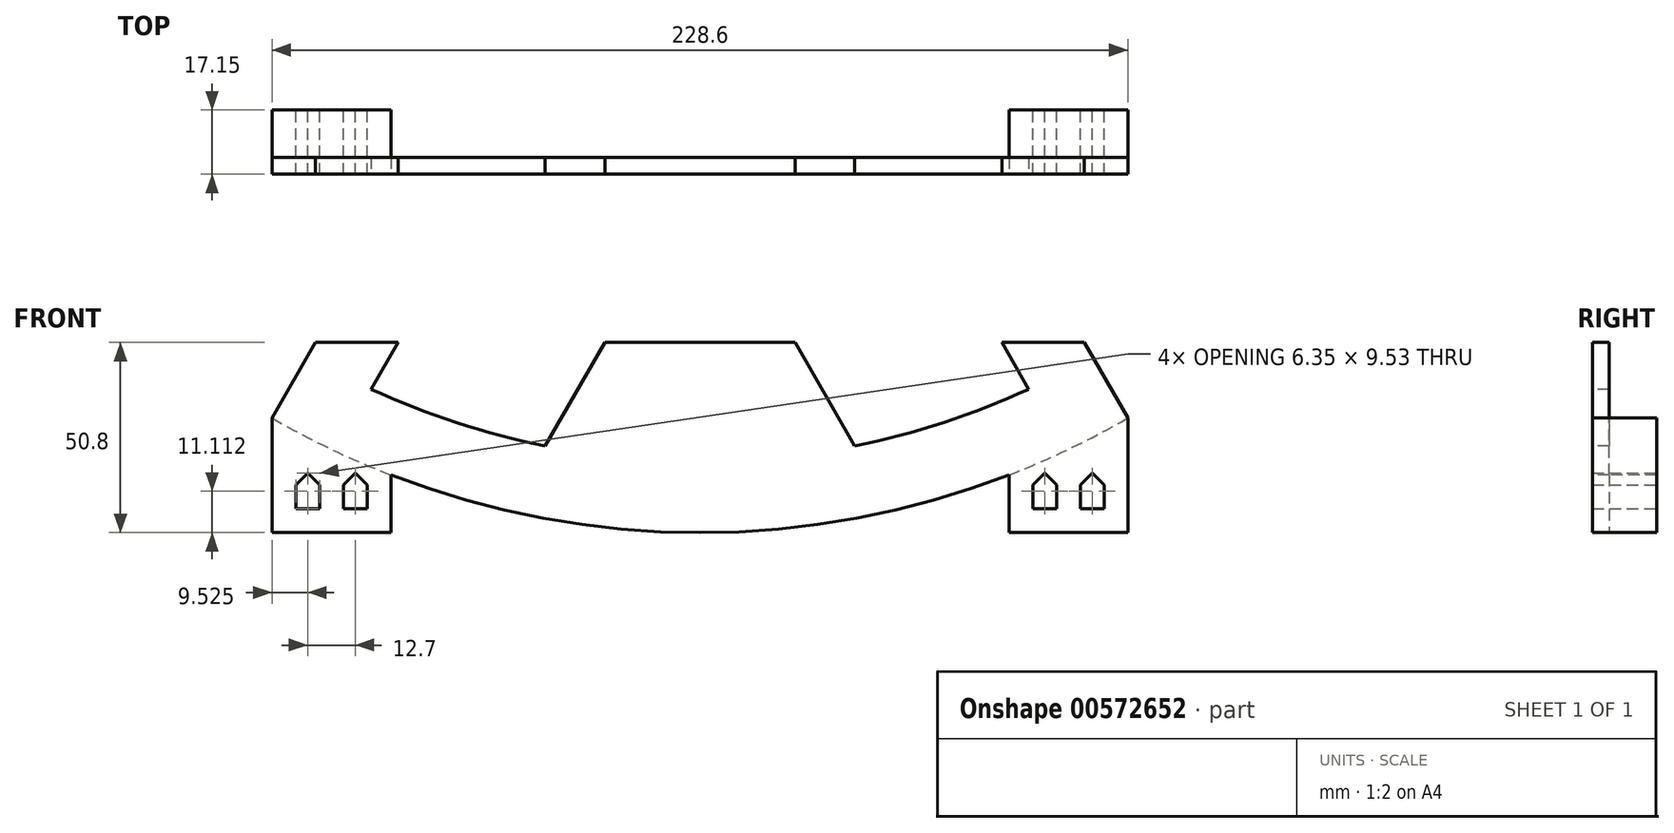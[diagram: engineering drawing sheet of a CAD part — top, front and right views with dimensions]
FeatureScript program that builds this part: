
annotation { "Feature Type Name" : "Feature", "Feature Type Description" : "" }
export const myFeature = defineFeature(function(context is Context, id is Id, definition is map)
    precondition{}
    {
        {
            var Q0;
            Q0=qCreatedBy(makeId("Front.planeOp"),FACE);
            var sketch = newSketch(context, id + "F0", { "sketchPlane" : qUnion([Q0])});
            skArc(sketch, "E0", {"start": v(-228.6, 0) * mm, "mid": v(0, -228.6) * mm, "end": v(228.6, 0) * mm});
            skLineSegment(sketch, "E1", {"start": v(-38.1, 0) * mm, "end": v(-228.6, 0) * mm});
            skLineSegment(sketch, "E2", {"start": v(38.1, 0) * mm, "end": v(228.6, 0) * mm});
            skLineSegment(sketch, "E3", {"start": v(-19.05, -33) * mm, "end": v(-114.3, -197.97) * mm});
            skLineSegment(sketch, "E4", {"start": v(19.05, -33) * mm, "end": v(114.3, -197.97) * mm});
            skArc(sketch, "E5", {"start": v(19.05, -33) * mm, "mid": v(0, 38.1) * mm, "end": v(-19.05, -33) * mm});
            skSolve(sketch);
        }
        {
            var Q0;
            {var subQ3=sQuery(id+"F0.wireOp",EDGE,"E3");Q0=makeQuery(id+"F0.imprint","IMPRINT",FACE,{"disambiguationData":[TD([[makeQuery(id+"F0.imprint","IMPRINT",EDGE,{"derivedFrom":subQ3}),1.0]])]});}
            extrude(context, id + "F1", {"entities" : qUnion([Q0]), "depth" : 127 * mm, "offsetDistance" : 25.4 * mm});
        }
        {
            var Q0;
            Q0=makeQuery(id+"F1.opExtrude","SWEPT_FACE",FACE,{"disambiguationData":[OSD([sQuery(id+"F0.wireOp",EDGE,"E5")])]});
            var Q1;
            Q1=makeQuery(id+"F1.opExtrude","SWEPT_FACE",FACE,{"disambiguationData":[OSD([sQuery(id+"F0.wireOp",EDGE,"E4")])]});
            var Q2;
            Q2=makeQuery(id+"F1.opExtrude","SWEPT_FACE",FACE,{"disambiguationData":[OSD([sQuery(id+"F0.wireOp",EDGE,"E3")])]});
            shell(context, id + "F2", {"entities" : qUnion([Q0, Q1, Q2]), "thickness" : 4.44 * mm});
        }
        {
            var Q0;
            Q0=makeQuery(id+"F1.opExtrude","CAP_FACE",FACE,{"disambiguationData":[OSD([sQuery(id+"F0.wireOp",EDGE,"E0"),sQuery(id+"F0.wireOp",EDGE,"E3"),sQuery(id+"F0.wireOp",EDGE,"E4"),sQuery(id+"F0.wireOp",EDGE,"E5")])],"isStart":false});
            var sketch = newSketch(context, id + "F3", { "sketchPlane" : qUnion([Q0])});
            skLineSegment(sketch, "E6.0", {"start": v(7.05, -50.3) * mm, "end": v(87.84, -190.25) * mm});
            skArc(sketch, "E6.1", {"start": v(-87.84, -190.25) * mm, "mid": v(-48.4, -203.88) * mm, "end": v(-7.05, -209.43) * mm});
            skCircle(sketch, "E7", {"center": v(0, 0) * mm, "radius": 9.53 * mm});
            skLineSegment(sketch, "E8", {"start": v(-7.05, -50.3) * mm, "end": v(-7.05, -125.9) * mm});
            skLineSegment(sketch, "E9", {"start": v(7.05, -50.3) * mm, "end": v(7.05, -125.9) * mm});
            skLineSegment(sketch, "E10", {"start": v(-87.84, -190.25) * mm, "end": v(-50.62, -125.78) * mm});
            skPoint(sketch, "E11.endSnap0", {"position": v(-66.67, -115.48) * mm});
            skLineSegment(sketch, "E12", {"start": v(-44.27, -114.78) * mm, "end": v(-14.9, -131.73) * mm});
            skLineSegment(sketch, "E13.trimOffspring", {"start": v(-7.05, -169.35) * mm, "end": v(-7.05, -209.43) * mm});
            skLineSegment(sketch, "E14.trimOffspring", {"start": v(-50.62, -125.78) * mm, "end": v(-87.84, -190.25) * mm});
            skArc(sketch, "E15.trimOffspring", {"start": v(7.05, -209.43) * mm, "mid": v(48.4, -203.88) * mm, "end": v(87.84, -190.25) * mm});
            skLineSegment(sketch, "E16", {"start": v(-7.05, -50.3) * mm, "end": v(0, -50.3) * mm, "construction": true});
            skLineSegment(sketch, "E17", {"start": v(0, -50.3) * mm, "end": v(0, -85.39) * mm, "construction": true});
            skLineSegment(sketch, "E18", {"start": v(-44.27, -114.78) * mm, "end": v(-7.05, -50.3) * mm});
            skLineSegment(sketch, "E19.MirrorCS", {"start": v(44.27, -114.78) * mm, "end": v(14.9, -131.73) * mm});
            skLineSegment(sketch, "E20.trimOffspring", {"start": v(7.05, -169.35) * mm, "end": v(7.05, -209.43) * mm});
            skArc(sketch, "E21", {"start": v(14.9, -131.73) * mm, "mid": v(11.36, -128.3) * mm, "end": v(7.05, -125.9) * mm});
            skPoint(sketch, "E22.orphan", {"position": v(7.05, -136.27) * mm});
            skPoint(sketch, "E23.orphan", {"position": v(7.05, -150.93) * mm});
            skPoint(sketch, "E24.orphan", {"position": v(-7.05, -150.93) * mm});
            skPoint(sketch, "E25.orphan", {"position": v(-7.05, -136.27) * mm});
            skLineSegment(sketch, "E26", {"start": v(50.62, -125.78) * mm, "end": v(7.05, -169.35) * mm, "construction": true});
            skLineSegment(sketch, "E27", {"start": v(50.62, -125.78) * mm, "end": v(7.05, -169.35) * mm});
            skLineSegment(sketch, "E28.MirrorCS", {"start": v(-50.62, -125.78) * mm, "end": v(-7.05, -169.35) * mm});
            skArc(sketch, "E29.trimOffspring", {"start": v(-7.05, -125.9) * mm, "mid": v(-11.36, -128.3) * mm, "end": v(-14.9, -131.73) * mm});
            skSolve(sketch);
        }
        {
            var Q0;
            Q0=makeQuery(id+"F3.imprint","IMPRINT",FACE,{"disambiguationData":[TD([[makeQuery(id+"F3.imprint","IMPRINT",EDGE,{"derivedFrom":sQuery(id+"F3.wireOp",EDGE,"E6.1")}),1.0]])]});
            var Q1;
            {var subQ2=sQuery(id+"F3.wireOp",EDGE,"E15.trimOffspring");Q1=makeQuery(id+"F3.imprint","IMPRINT",FACE,{"disambiguationData":[TD([[makeQuery(id+"F3.imprint","IMPRINT",EDGE,{"derivedFrom":subQ2}),1.0]])]});}
            var Q2;
            {var subQ0=sQuery(id+"F3.wireOp",EDGE,"E9");Q2=makeQuery(id+"F3.imprint","IMPRINT",FACE,{"disambiguationData":[TD([[makeQuery(id+"F3.imprint","IMPRINT",EDGE,{"derivedFrom":subQ0}),1.0]])]});}
            var Q3;
            {var subQ0=sQuery(id+"F3.wireOp",EDGE,"E8");Q3=makeQuery(id+"F3.imprint","IMPRINT",FACE,{"disambiguationData":[TD([[makeQuery(id+"F3.imprint","IMPRINT",EDGE,{"derivedFrom":subQ0}),-1.0]])]});}
            var Q4;
            Q4=makeQuery(id+"F3.imprint","IMPRINT",FACE,{"disambiguationData":[TD([[makeQuery(id+"F3.imprint","IMPRINT",EDGE,{"derivedFrom":sQuery(id+"F3.wireOp",EDGE,"E7")}),1.0]])]});
            var Q5;
            Q5=makeQuery(id+"F1.opExtrude","CAP_FACE",FACE,{"disambiguationData":[OSD([sQuery(id+"F0.wireOp",EDGE,"E0"),sQuery(id+"F0.wireOp",EDGE,"E3"),sQuery(id+"F0.wireOp",EDGE,"E4"),sQuery(id+"F0.wireOp",EDGE,"E5")])],"isStart":true});
            extrude(context, id + "F4", {"entities" : qUnion([Q0, Q1, Q2, Q3, Q4]), "operationType" : NewBodyOperationType.REMOVE, "endBound" : BoundingType.UP_TO_SURFACE, "oppositeDirection" : true, "depth" : 25.4 * mm, "endBoundEntityFace" : qUnion([Q5]), "offsetDistance" : 25.4 * mm});
        }
        {
            var Q0;
            Q0=qCreatedBy(makeId("Front.planeOp"),FACE);
            var sketch = newSketch(context, id + "F5", { "sketchPlane" : qUnion([Q0])});
            skLineSegment(sketch, "E30", {"start": v(0, -228.6) * mm, "end": v(114.3, -228.6) * mm});
            skLineSegment(sketch, "E31", {"start": v(0, -228.6) * mm, "end": v(-114.3, -228.6) * mm});
            skLineSegment(sketch, "E32", {"start": v(114.3, -197.97) * mm, "end": v(114.3, -228.6) * mm});
            skLineSegment(sketch, "E33", {"start": v(-114.3, -197.97) * mm, "end": v(-114.3, -228.6) * mm});
            skPoint(sketch, "E34.orphan", {"position": v(-122.47, -228.6) * mm});
            skArc(sketch, "E35.0", {"start": v(-114.3, -197.97) * mm, "mid": v(0, -228.6) * mm, "end": v(114.3, -197.97) * mm});
            skLineSegment(sketch, "E36", {"start": v(114.3, -228.6) * mm, "end": v(107.95, -228.6) * mm, "construction": true});
            skLineSegment(sketch, "E37", {"start": v(107.95, -228.6) * mm, "end": v(107.95, -222.25) * mm, "construction": true});
            skLineSegment(sketch, "E38.bottom", {"start": v(107.95, -222.25) * mm, "end": v(101.6, -222.25) * mm});
            skLineSegment(sketch, "E38.left", {"start": v(107.95, -222.25) * mm, "end": v(107.95, -215.9) * mm});
            skLineSegment(sketch, "E38.right", {"start": v(88.9, -222.25) * mm, "end": v(88.9, -215.9) * mm});
            skLineSegment(sketch, "E39", {"start": v(101.6, -222.25) * mm, "end": v(101.6, -215.9) * mm});
            skLineSegment(sketch, "E40", {"start": v(95.25, -222.25) * mm, "end": v(95.25, -215.9) * mm});
            skLineSegment(sketch, "E41.trimOffspring", {"start": v(95.25, -222.25) * mm, "end": v(88.9, -222.25) * mm});
            skLineSegment(sketch, "E42", {"start": v(104.78, -215.9) * mm, "end": v(104.78, -212.72) * mm, "construction": true});
            skLineSegment(sketch, "E43", {"start": v(92.08, -215.9) * mm, "end": v(92.08, -212.72) * mm, "construction": true});
            skLineSegment(sketch, "E44", {"start": v(107.95, -215.9) * mm, "end": v(104.78, -212.72) * mm});
            skLineSegment(sketch, "E45", {"start": v(101.6, -215.9) * mm, "end": v(104.78, -212.72) * mm});
            skLineSegment(sketch, "E46", {"start": v(95.25, -215.9) * mm, "end": v(92.08, -212.72) * mm});
            skLineSegment(sketch, "E47", {"start": v(88.9, -215.9) * mm, "end": v(92.08, -212.72) * mm});
            skLineSegment(sketch, "E48.MirrorCS", {"start": v(-104.78, -215.9) * mm, "end": v(-104.78, -212.72) * mm, "construction": true});
            skLineSegment(sketch, "E49.MirrorCS", {"start": v(-92.08, -215.9) * mm, "end": v(-92.08, -212.72) * mm, "construction": true});
            skLineSegment(sketch, "E50.MirrorCS", {"start": v(-101.6, -215.9) * mm, "end": v(-104.78, -212.72) * mm});
            skLineSegment(sketch, "E51.MirrorCS", {"start": v(-88.9, -215.9) * mm, "end": v(-92.08, -212.72) * mm});
            skLineSegment(sketch, "E52.MirrorCS", {"start": v(-107.95, -215.9) * mm, "end": v(-104.78, -212.72) * mm});
            skLineSegment(sketch, "E53.MirrorCS", {"start": v(-95.25, -222.25) * mm, "end": v(-95.25, -215.9) * mm});
            skLineSegment(sketch, "E54.MirrorCS", {"start": v(-101.6, -222.25) * mm, "end": v(-101.6, -215.9) * mm});
            skLineSegment(sketch, "E55.MirrorCS", {"start": v(-107.95, -222.25) * mm, "end": v(-107.95, -215.9) * mm});
            skLineSegment(sketch, "E56.MirrorCS", {"start": v(-107.95, -222.25) * mm, "end": v(-101.6, -222.25) * mm});
            skLineSegment(sketch, "E57.MirrorCS", {"start": v(-88.9, -222.25) * mm, "end": v(-88.9, -215.9) * mm});
            skLineSegment(sketch, "E58.MirrorCS", {"start": v(-95.25, -215.9) * mm, "end": v(-92.08, -212.72) * mm});
            skLineSegment(sketch, "E59.MirrorCS", {"start": v(-95.25, -222.25) * mm, "end": v(-88.9, -222.25) * mm});
            skSolve(sketch);
        }
        {
            var Q0;
            {var subQ2=sQuery(id+"F5.wireOp",EDGE,"E30");Q0=makeQuery(id+"F5.imprint","IMPRINT",FACE,{"disambiguationData":[TD([[makeQuery(id+"F5.imprint","IMPRINT",EDGE,{"derivedFrom":subQ2}),1.0]])]});}
            var Q1;
            {var subQ2=sQuery(id+"F5.wireOp",EDGE,"E31");Q1=makeQuery(id+"F5.imprint","IMPRINT",FACE,{"disambiguationData":[TD([[makeQuery(id+"F5.imprint","IMPRINT",EDGE,{"derivedFrom":subQ2}),-1.0]])]});}
            var Q2;
            Q2=makeQuery(id+"F1.opExtrude","CAP_FACE",FACE,{"disambiguationData":[OSD([sQuery(id+"F0.wireOp",EDGE,"E0"),sQuery(id+"F0.wireOp",EDGE,"E3"),sQuery(id+"F0.wireOp",EDGE,"E4"),sQuery(id+"F0.wireOp",EDGE,"E5")])],"isStart":false});
            extrude(context, id + "F6", {"entities" : qUnion([Q0, Q1]), "operationType" : NewBodyOperationType.ADD, "endBound" : BoundingType.UP_TO_SURFACE, "depth" : 25.4 * mm, "endBoundEntityFace" : qUnion([Q2]), "offsetDistance" : 25.4 * mm});
        }
        {
            var Q0;
            Q0=qCreatedBy(makeId("Front.planeOp"),FACE);
            var sketch = newSketch(context, id + "F7", { "sketchPlane" : qUnion([Q0])});
            skLineSegment(sketch, "E60", {"start": v(0, 0) * mm, "end": v(0, -177.8) * mm, "construction": true});
            skLineSegment(sketch, "E61", {"start": v(0, -177.8) * mm, "end": v(122.5, -177.8) * mm});
            skLineSegment(sketch, "E62", {"start": v(122.5, -177.8) * mm, "end": v(122.5, 99.95) * mm});
            skLineSegment(sketch, "E63", {"start": v(0, -177.8) * mm, "end": v(-155.13, -177.8) * mm});
            skLineSegment(sketch, "E64", {"start": v(-155.13, -177.8) * mm, "end": v(-155.13, 97.68) * mm});
            skLineSegment(sketch, "E65", {"start": v(-155.13, 97.68) * mm, "end": v(122.5, 99.95) * mm});
            skSolve(sketch);
        }
        {
            var Q0;
            Q0=makeQuery(id+"F7.imprint","IMPRINT",FACE,{"disambiguationData":[TD([[makeQuery(id+"F7.imprint","IMPRINT",EDGE,{"derivedFrom":sQuery(id+"F7.wireOp",EDGE,"E61")}),1.0]])]});
            extrude(context, id + "F8", {"entities" : qUnion([Q0]), "operationType" : NewBodyOperationType.REMOVE, "depth" : 154.94 * mm, "offsetDistance" : 25.4 * mm});
        }
        {
            var Q0;
            {var subQ0=sQuery(id+"F5.wireOp",EDGE,"E35.0");Q0=makeQuery(id+"F6.boolean.opBoolean","MERGE",FACE,{"derivedFrom":[makeQuery(id+"F1.opExtrude","CAP_FACE",FACE,{"disambiguationData":[OSD([sQuery(id+"F0.wireOp",EDGE,"E0"),sQuery(id+"F0.wireOp",EDGE,"E3"),sQuery(id+"F0.wireOp",EDGE,"E4"),sQuery(id+"F0.wireOp",EDGE,"E5")])],"isStart":true}),makeQuery(id+"F6.opExtrude","CAP_FACE",FACE,{"disambiguationData":[OSD([sQuery(id+"F5.wireOp",EDGE,"E30"),sQuery(id+"F5.wireOp",EDGE,"E32"),subQ0,sQuery(id+"F5.wireOp",EDGE,"E38.bottom"),sQuery(id+"F5.wireOp",EDGE,"E38.left"),sQuery(id+"F5.wireOp",EDGE,"E38.right"),sQuery(id+"F5.wireOp",EDGE,"E39"),sQuery(id+"F5.wireOp",EDGE,"E40"),sQuery(id+"F5.wireOp",EDGE,"E41.trimOffspring"),sQuery(id+"F5.wireOp",EDGE,"E44"),sQuery(id+"F5.wireOp",EDGE,"E45"),sQuery(id+"F5.wireOp",EDGE,"E46"),sQuery(id+"F5.wireOp",EDGE,"E47")])],"isStart":true}),makeQuery(id+"F6.opExtrude","CAP_FACE",FACE,{"disambiguationData":[OSD([sQuery(id+"F5.wireOp",EDGE,"E31"),sQuery(id+"F5.wireOp",EDGE,"E33"),subQ0,sQuery(id+"F5.wireOp",EDGE,"E50.MirrorCS"),sQuery(id+"F5.wireOp",EDGE,"E51.MirrorCS"),sQuery(id+"F5.wireOp",EDGE,"E52.MirrorCS"),sQuery(id+"F5.wireOp",EDGE,"E53.MirrorCS"),sQuery(id+"F5.wireOp",EDGE,"E54.MirrorCS"),sQuery(id+"F5.wireOp",EDGE,"E55.MirrorCS"),sQuery(id+"F5.wireOp",EDGE,"E56.MirrorCS"),sQuery(id+"F5.wireOp",EDGE,"E57.MirrorCS"),sQuery(id+"F5.wireOp",EDGE,"E58.MirrorCS"),sQuery(id+"F5.wireOp",EDGE,"E59.MirrorCS")])],"isStart":true})]});}
            var sketch = newSketch(context, id + "F9", { "sketchPlane" : qUnion([Q0])});
            skArc(sketch, "E66.0", {"start": v(-87.84, -190.25) * mm, "mid": v(-48.4, -203.88) * mm, "end": v(-7.05, -209.43) * mm});
            skLineSegment(sketch, "E67.0", {"start": v(-7.05, -209.43) * mm, "end": v(-7.05, -177.8) * mm});
            skLineSegment(sketch, "E68", {"start": v(0, -177.8) * mm, "end": v(25.4, -177.8) * mm});
            skLineSegment(sketch, "E69", {"start": v(0, -177.8) * mm, "end": v(-25.4, -177.8) * mm});
            skLineSegment(sketch, "E70", {"start": v(-25.4, -177.8) * mm, "end": v(-41.35, -205.43) * mm});
            skLineSegment(sketch, "E71", {"start": v(25.4, -177.8) * mm, "end": v(41.35, -205.43) * mm});
            skLineSegment(sketch, "E72.0", {"start": v(7.05, -209.43) * mm, "end": v(7.05, -177.8) * mm});
            skArc(sketch, "E73.0", {"start": v(7.05, -209.43) * mm, "mid": v(48.4, -203.88) * mm, "end": v(87.84, -190.25) * mm});
            skSolve(sketch);
        }
        {
            var Q0;
            {var subQ0=sQuery(id+"F9.wireOp",EDGE,"E67.0");Q0=makeQuery(id+"F9.imprint","IMPRINT",FACE,{"disambiguationData":[TD([[makeQuery(id+"F9.imprint","IMPRINT",EDGE,{"derivedFrom":subQ0}),1.0]])]});}
            var Q1;
            {var subQ2=sQuery(id+"F9.wireOp",EDGE,"E71");Q1=makeQuery(id+"F9.imprint","IMPRINT",FACE,{"disambiguationData":[TD([[makeQuery(id+"F9.imprint","IMPRINT",EDGE,{"derivedFrom":subQ2}),-1.0]])]});}
            var Q2;
            {var subQ0=sQuery(id+"F0.wireOp",EDGE,"E5");var subQ1=sQuery(id+"F0.wireOp",EDGE,"E4");var subQ2=sQuery(id+"F0.wireOp",EDGE,"E3");var subQ3=sQuery(id+"F0.wireOp",EDGE,"E0");Q2=makeQuery(id+"F2.opShell","OFFSET_FACE",FACE,{"disambiguationData":[OSD([subQ3,subQ2,subQ1,subQ0]),TDD([makeQuery(id+"F1.opExtrude","CAP_FACE",FACE,{"disambiguationData":[OSD([subQ3,subQ2,subQ1,subQ0])],"isStart":true})])]});}
            extrude(context, id + "F10", {"entities" : qUnion([Q0, Q1]), "operationType" : NewBodyOperationType.ADD, "endBound" : BoundingType.UP_TO_SURFACE, "oppositeDirection" : true, "depth" : 25.4 * mm, "endBoundEntityFace" : qUnion([Q2]), "offsetDistance" : 25.4 * mm});
        }
        {
            var Q0;
            Q0=qCreatedBy(makeId("Front.planeOp"),FACE);
            var Q1;
            {var subQ0=sQuery(id+"F0.wireOp",EDGE,"E5");var subQ1=sQuery(id+"F0.wireOp",EDGE,"E4");var subQ2=sQuery(id+"F0.wireOp",EDGE,"E3");var subQ3=sQuery(id+"F0.wireOp",EDGE,"E0");Q1=makeQuery(id+"F6.boolean.opBoolean","MERGE",FACE,{"derivedFrom":[makeQuery(id+"F1.opExtrude","CAP_FACE",FACE,{"disambiguationData":[OSD([subQ3,subQ2,subQ1,subQ0])],"isStart":false}),makeQuery(id+"F6.opExtrude","CAP_FACE",FACE,{"disambiguationData":[OSD([subQ3,subQ2,subQ1,subQ0]),OD(0.0)],"isStart":false}),makeQuery(id+"F6.opExtrude","CAP_FACE",FACE,{"disambiguationData":[OSD([subQ3,subQ2,subQ1,subQ0]),OD(1.0)],"isStart":false})]});}
            cPlane(context, id + "F11", {"entities" : qUnion([Q0, Q1]), "cplaneType" : CPlaneType.MID_PLANE, "offset" : 25.4 * mm, "width" : 152.4 * mm, "height" : 152.4 * mm});
        }
        {
            var Q0;
            Q0=makeQuery(id+"F1.opExtrude","SWEPT_BODY",BODY,{"disambiguationData":[OSD([sQuery(id+"F0.wireOp",EDGE,"E0"),sQuery(id+"F0.wireOp",EDGE,"E3"),sQuery(id+"F0.wireOp",EDGE,"E4"),sQuery(id+"F0.wireOp",EDGE,"E5")])]});
            var Q1;
            Q1=qCreatedBy(id+"F11.planeOp",FACE);
            mirror(context, id + "F12", {"operationType" : NewBodyOperationType.ADD, "entities" : qUnion([Q0]), "mirrorPlane" : qUnion([Q1])});
        }
        {
            var Q0;
            {var subQ0=sQuery(id+"F5.wireOp",EDGE,"E35.0");var subQ1=sQuery(id+"F0.wireOp",EDGE,"E5");var subQ2=sQuery(id+"F0.wireOp",EDGE,"E4");var subQ3=sQuery(id+"F0.wireOp",EDGE,"E3");var subQ4=sQuery(id+"F0.wireOp",EDGE,"E0");Q0=makeQuery(id+"F12.boolean.opBoolean","MERGE",FACE,{"derivedFrom":[makeQuery(id+"F6.boolean.opBoolean","MERGE",FACE,{"derivedFrom":[makeQuery(id+"F1.opExtrude","CAP_FACE",FACE,{"disambiguationData":[OSD([subQ4,subQ3,subQ2,subQ1])],"isStart":false}),makeQuery(id+"F6.opExtrude","CAP_FACE",FACE,{"disambiguationData":[OSD([subQ4,subQ3,subQ2,subQ1]),OD(0.0)],"isStart":false}),makeQuery(id+"F6.opExtrude","CAP_FACE",FACE,{"disambiguationData":[OSD([subQ4,subQ3,subQ2,subQ1]),OD(1.0)],"isStart":false})]}),makeQuery(id+"F12.opPattern","COPY",FACE,{"derivedFrom":makeQuery(id+"F10.boolean.opBoolean","MERGE",FACE,{"derivedFrom":[makeQuery(id+"F6.boolean.opBoolean","MERGE",FACE,{"derivedFrom":[makeQuery(id+"F1.opExtrude","CAP_FACE",FACE,{"disambiguationData":[OSD([subQ4,subQ3,subQ2,subQ1])],"isStart":true}),makeQuery(id+"F6.opExtrude","CAP_FACE",FACE,{"disambiguationData":[OSD([sQuery(id+"F5.wireOp",EDGE,"E30"),sQuery(id+"F5.wireOp",EDGE,"E32"),subQ0,sQuery(id+"F5.wireOp",EDGE,"E38.bottom"),sQuery(id+"F5.wireOp",EDGE,"E38.left"),sQuery(id+"F5.wireOp",EDGE,"E38.right"),sQuery(id+"F5.wireOp",EDGE,"E39"),sQuery(id+"F5.wireOp",EDGE,"E40"),sQuery(id+"F5.wireOp",EDGE,"E41.trimOffspring"),sQuery(id+"F5.wireOp",EDGE,"E44"),sQuery(id+"F5.wireOp",EDGE,"E45"),sQuery(id+"F5.wireOp",EDGE,"E46"),sQuery(id+"F5.wireOp",EDGE,"E47")])],"isStart":true}),makeQuery(id+"F6.opExtrude","CAP_FACE",FACE,{"disambiguationData":[OSD([sQuery(id+"F5.wireOp",EDGE,"E31"),sQuery(id+"F5.wireOp",EDGE,"E33"),subQ0,sQuery(id+"F5.wireOp",EDGE,"E50.MirrorCS"),sQuery(id+"F5.wireOp",EDGE,"E51.MirrorCS"),sQuery(id+"F5.wireOp",EDGE,"E52.MirrorCS"),sQuery(id+"F5.wireOp",EDGE,"E53.MirrorCS"),sQuery(id+"F5.wireOp",EDGE,"E54.MirrorCS"),sQuery(id+"F5.wireOp",EDGE,"E55.MirrorCS"),sQuery(id+"F5.wireOp",EDGE,"E56.MirrorCS"),sQuery(id+"F5.wireOp",EDGE,"E57.MirrorCS"),sQuery(id+"F5.wireOp",EDGE,"E58.MirrorCS"),sQuery(id+"F5.wireOp",EDGE,"E59.MirrorCS")])],"isStart":true})]}),makeQuery(id+"F10.opExtrude","CAP_FACE",FACE,{"disambiguationData":[OSD([sQuery(id+"F9.wireOp",EDGE,"E66.0"),sQuery(id+"F9.wireOp",EDGE,"E67.0"),sQuery(id+"F9.wireOp",EDGE,"E69"),sQuery(id+"F9.wireOp",EDGE,"E70")])],"isStart":true}),makeQuery(id+"F10.opExtrude","CAP_FACE",FACE,{"disambiguationData":[OSD([sQuery(id+"F9.wireOp",EDGE,"E68"),sQuery(id+"F9.wireOp",EDGE,"E71"),sQuery(id+"F9.wireOp",EDGE,"E72.0"),sQuery(id+"F9.wireOp",EDGE,"E73.0")])],"isStart":true})]}),"instanceName":"1"})]});}
            var sketch = newSketch(context, id + "F13", { "sketchPlane" : qUnion([Q0])});
            skArc(sketch, "E74", {"start": v(-114.3, -197.97) * mm, "mid": v(0, -228.6) * mm, "end": v(114.3, -197.97) * mm});
            skLineSegment(sketch, "E75.0", {"start": v(114.3, -228.6) * mm, "end": v(-114.3, -228.6) * mm});
            skLineSegment(sketch, "E76", {"start": v(-82.55, -228.6) * mm, "end": v(-82.55, -213.17) * mm});
            skLineSegment(sketch, "E77.MirrorCS", {"start": v(82.55, -228.6) * mm, "end": v(82.55, -213.17) * mm});
            skArc(sketch, "E78.MirrorCS", {"start": v(114.3, -197.97) * mm, "mid": v(0, -228.6) * mm, "end": v(-114.3, -197.97) * mm});
            skLineSegment(sketch, "E79.MirrorCS", {"start": v(-114.3, -228.6) * mm, "end": v(114.3, -228.6) * mm});
            skSolve(sketch);
        }
        {
            var Q0;
            {var subQ0=sQuery(id+"F13.wireOp",EDGE,"E76");Q0=makeQuery(id+"F13.imprint","IMPRINT",FACE,{"disambiguationData":[TD([[makeQuery(id+"F13.imprint","IMPRINT",EDGE,{"derivedFrom":subQ0}),-1.0]])]});}
            var Q1;
            {var subQ0=sQuery(id+"F13.wireOp",EDGE,"E77.MirrorCS");Q1=makeQuery(id+"F13.imprint","IMPRINT",FACE,{"disambiguationData":[TD([[makeQuery(id+"F13.imprint","IMPRINT",EDGE,{"derivedFrom":subQ0}),1.0]])]});}
            var Q2;
            {var subQ0=sQuery(id+"F5.wireOp",EDGE,"E35.0");Q2=makeQuery(id+"F10.boolean.opBoolean","MERGE",FACE,{"derivedFrom":[makeQuery(id+"F6.boolean.opBoolean","MERGE",FACE,{"derivedFrom":[makeQuery(id+"F1.opExtrude","CAP_FACE",FACE,{"disambiguationData":[OSD([sQuery(id+"F0.wireOp",EDGE,"E0"),sQuery(id+"F0.wireOp",EDGE,"E3"),sQuery(id+"F0.wireOp",EDGE,"E4"),sQuery(id+"F0.wireOp",EDGE,"E5")])],"isStart":true}),makeQuery(id+"F6.opExtrude","CAP_FACE",FACE,{"disambiguationData":[OSD([sQuery(id+"F5.wireOp",EDGE,"E30"),sQuery(id+"F5.wireOp",EDGE,"E32"),subQ0,sQuery(id+"F5.wireOp",EDGE,"E38.bottom"),sQuery(id+"F5.wireOp",EDGE,"E38.left"),sQuery(id+"F5.wireOp",EDGE,"E38.right"),sQuery(id+"F5.wireOp",EDGE,"E39"),sQuery(id+"F5.wireOp",EDGE,"E40"),sQuery(id+"F5.wireOp",EDGE,"E41.trimOffspring"),sQuery(id+"F5.wireOp",EDGE,"E44"),sQuery(id+"F5.wireOp",EDGE,"E45"),sQuery(id+"F5.wireOp",EDGE,"E46"),sQuery(id+"F5.wireOp",EDGE,"E47")])],"isStart":true}),makeQuery(id+"F6.opExtrude","CAP_FACE",FACE,{"disambiguationData":[OSD([sQuery(id+"F5.wireOp",EDGE,"E31"),sQuery(id+"F5.wireOp",EDGE,"E33"),subQ0,sQuery(id+"F5.wireOp",EDGE,"E50.MirrorCS"),sQuery(id+"F5.wireOp",EDGE,"E51.MirrorCS"),sQuery(id+"F5.wireOp",EDGE,"E52.MirrorCS"),sQuery(id+"F5.wireOp",EDGE,"E53.MirrorCS"),sQuery(id+"F5.wireOp",EDGE,"E54.MirrorCS"),sQuery(id+"F5.wireOp",EDGE,"E55.MirrorCS"),sQuery(id+"F5.wireOp",EDGE,"E56.MirrorCS"),sQuery(id+"F5.wireOp",EDGE,"E57.MirrorCS"),sQuery(id+"F5.wireOp",EDGE,"E58.MirrorCS"),sQuery(id+"F5.wireOp",EDGE,"E59.MirrorCS")])],"isStart":true})]}),makeQuery(id+"F10.opExtrude","CAP_FACE",FACE,{"disambiguationData":[OSD([sQuery(id+"F9.wireOp",EDGE,"E66.0"),sQuery(id+"F9.wireOp",EDGE,"E67.0"),sQuery(id+"F9.wireOp",EDGE,"E69"),sQuery(id+"F9.wireOp",EDGE,"E70")])],"isStart":true}),makeQuery(id+"F10.opExtrude","CAP_FACE",FACE,{"disambiguationData":[OSD([sQuery(id+"F9.wireOp",EDGE,"E68"),sQuery(id+"F9.wireOp",EDGE,"E71"),sQuery(id+"F9.wireOp",EDGE,"E72.0"),sQuery(id+"F9.wireOp",EDGE,"E73.0")])],"isStart":true})]});}
            extrude(context, id + "F14", {"entities" : qUnion([Q0, Q1]), "operationType" : NewBodyOperationType.REMOVE, "endBound" : BoundingType.UP_TO_SURFACE, "oppositeDirection" : true, "depth" : 25.4 * mm, "endBoundEntityFace" : qUnion([Q2]), "offsetDistance" : 25.4 * mm});
        }
        {
            var Q0;
            Q0=qCreatedBy(makeId("Top.planeOp"),FACE);
            var sketch = newSketch(context, id + "F15", { "sketchPlane" : qUnion([Q0])});
            skPoint(sketch, "E80.0", {"position": v(-112.08, -4.45) * mm});
            skPoint(sketch, "E81.0", {"position": v(112.08, -4.45) * mm});
            skPoint(sketch, "E82.0", {"position": v(112.08, -122.55) * mm});
            skPoint(sketch, "E83.0", {"position": v(-112.08, -122.55) * mm});
            skLineSegment(sketch, "E84.0", {"start": v(-114.3, -122.55) * mm, "end": v(-114.3, -4.45) * mm});
            skLineSegment(sketch, "E85.0", {"start": v(114.3, -122.55) * mm, "end": v(114.3, -4.45) * mm});
            skLineSegment(sketch, "E86", {"start": v(114.3, -122.55) * mm, "end": v(-114.3, -122.55) * mm});
            skPoint(sketch, "E87.orphan", {"position": v(114.3, -127) * mm});
            skPoint(sketch, "E88.orphan", {"position": v(-114.3, -127) * mm});
            skPoint(sketch, "E89.orphan", {"position": v(114.3, 0) * mm});
            skPoint(sketch, "E90.orphan", {"position": v(-114.3, 0) * mm});
            skLineSegment(sketch, "E91", {"start": v(-114.3, -4.45) * mm, "end": v(-114.3, 0) * mm});
            skLineSegment(sketch, "E92", {"start": v(-114.3, 0) * mm, "end": v(114.3, 0) * mm});
            skLineSegment(sketch, "E93", {"start": v(114.3, 0) * mm, "end": v(114.3, -4.45) * mm});
            skSolve(sketch);
        }
        {
            var Q0;
            Q0=qSketchRegion(id+"F15",true);
            extrude(context, id + "F16", {"entities" : qUnion([Q0]), "operationType" : NewBodyOperationType.REMOVE, "oppositeDirection" : true, "depth" : 279.4 * mm, "offsetDistance" : 25.4 * mm});
        }
        {
            var Q0;
            {var subQ0=sQuery(id+"F0.wireOp",EDGE,"E5");var subQ1=sQuery(id+"F0.wireOp",EDGE,"E4");var subQ2=sQuery(id+"F0.wireOp",EDGE,"E3");var subQ3=sQuery(id+"F0.wireOp",EDGE,"E0");Q0=makeQuery(id+"F16.boolean.opBoolean","MERGE",FACE,{"derivedFrom":[makeQuery(id+"F12.boolean.opBoolean","MERGE",FACE,{"derivedFrom":[makeQuery(id+"F2.opShell","OFFSET_FACE",FACE,{"disambiguationData":[OSD([subQ3,subQ2,subQ1,subQ0]),TDD([makeQuery(id+"F1.opExtrude","CAP_FACE",FACE,{"disambiguationData":[OSD([subQ3,subQ2,subQ1,subQ0])],"isStart":false})])]}),makeQuery(id+"F12.opPattern","COPY",FACE,{"derivedFrom":makeQuery(id+"F10.boolean.opBoolean","MERGE",FACE,{"derivedFrom":[makeQuery(id+"F2.opShell","OFFSET_FACE",FACE,{"disambiguationData":[OSD([subQ3,subQ2,subQ1,subQ0]),TDD([makeQuery(id+"F1.opExtrude","CAP_FACE",FACE,{"disambiguationData":[OSD([subQ3,subQ2,subQ1,subQ0])],"isStart":true})])]}),makeQuery(id+"F10.opExtrude","CAP_FACE",FACE,{"disambiguationData":[OSD([subQ3,subQ2,subQ1,subQ0]),OD(0.0)],"isStart":false}),makeQuery(id+"F10.opExtrude","CAP_FACE",FACE,{"disambiguationData":[OSD([subQ3,subQ2,subQ1,subQ0]),OD(1.0)],"isStart":false})]}),"instanceName":"1"})]}),makeQuery(id+"F16.opExtrude","SWEPT_FACE",FACE,{"disambiguationData":[OSD([sQuery(id+"F15.wireOp",EDGE,"E86")])]})]});}
            var sketch = newSketch(context, id + "F17", { "sketchPlane" : qUnion([Q0])});
            skArc(sketch, "E94", {"start": v(-114.3, -197.97) * mm, "mid": v(-98.72, -206.19) * mm, "end": v(-82.55, -213.17) * mm});
            skLineSegment(sketch, "E95.0", {"start": v(-82.55, -228.6) * mm, "end": v(-114.3, -228.6) * mm});
            skLineSegment(sketch, "E96.0", {"start": v(-114.3, -228.6) * mm, "end": v(-114.3, -197.97) * mm});
            skLineSegment(sketch, "E97.0", {"start": v(-82.55, -228.6) * mm, "end": v(-82.55, -213.17) * mm});
            skPoint(sketch, "E98.0", {"position": v(-92.08, -222.25) * mm});
            skLineSegment(sketch, "E99.0", {"start": v(-95.25, -215.9) * mm, "end": v(-95.25, -222.25) * mm});
            skPoint(sketch, "E100.0", {"position": v(-93.66, -214.31) * mm});
            skLineSegment(sketch, "E101.0", {"start": v(-92.08, -212.72) * mm, "end": v(-88.9, -215.9) * mm});
            skLineSegment(sketch, "E102.0", {"start": v(-88.9, -215.9) * mm, "end": v(-88.9, -222.25) * mm});
            skPoint(sketch, "E103.0", {"position": v(-103.19, -214.31) * mm});
            skLineSegment(sketch, "E104.0", {"start": v(-104.78, -212.72) * mm, "end": v(-101.6, -215.9) * mm});
            skLineSegment(sketch, "E105.0", {"start": v(-104.78, -212.72) * mm, "end": v(-107.95, -215.9) * mm});
            skLineSegment(sketch, "E106.0", {"start": v(-107.95, -215.9) * mm, "end": v(-107.95, -222.25) * mm});
            skLineSegment(sketch, "E107.0", {"start": v(-101.6, -222.25) * mm, "end": v(-107.95, -222.25) * mm});
            skLineSegment(sketch, "E108.0", {"start": v(-101.6, -215.9) * mm, "end": v(-101.6, -222.25) * mm});
            skLineSegment(sketch, "E109.MirrorCS", {"start": v(101.6, -222.25) * mm, "end": v(107.95, -222.25) * mm});
            skLineSegment(sketch, "E110.MirrorCS", {"start": v(104.78, -212.72) * mm, "end": v(107.95, -215.9) * mm});
            skLineSegment(sketch, "E111.MirrorCS", {"start": v(101.6, -215.9) * mm, "end": v(101.6, -222.25) * mm});
            skLineSegment(sketch, "E112.MirrorCS", {"start": v(107.95, -215.9) * mm, "end": v(107.95, -222.25) * mm});
            skLineSegment(sketch, "E113.MirrorCS", {"start": v(104.78, -212.72) * mm, "end": v(101.6, -215.9) * mm});
            skLineSegment(sketch, "E114.MirrorCS", {"start": v(92.08, -212.72) * mm, "end": v(88.9, -215.9) * mm});
            skLineSegment(sketch, "E115.MirrorCS", {"start": v(95.25, -215.9) * mm, "end": v(95.25, -222.25) * mm});
            skLineSegment(sketch, "E116.MirrorCS", {"start": v(88.9, -215.9) * mm, "end": v(88.9, -222.25) * mm});
            skPoint(sketch, "E117.MirrorP", {"position": v(92.08, -222.25) * mm});
            skLineSegment(sketch, "E118.MirrorCS", {"start": v(82.55, -228.6) * mm, "end": v(114.3, -228.6) * mm});
            skArc(sketch, "E119.MirrorCS", {"start": v(114.3, -197.97) * mm, "mid": v(98.72, -206.19) * mm, "end": v(82.55, -213.17) * mm});
            skPoint(sketch, "E120.MirrorP", {"position": v(103.19, -214.31) * mm});
            skLineSegment(sketch, "E121.MirrorCS", {"start": v(82.55, -228.6) * mm, "end": v(82.55, -213.17) * mm});
            skPoint(sketch, "E122.MirrorP", {"position": v(93.66, -214.31) * mm});
            skLineSegment(sketch, "E123.MirrorCS", {"start": v(114.3, -228.6) * mm, "end": v(114.3, -197.97) * mm});
            skLineSegment(sketch, "E124.0", {"start": v(92.08, -212.72) * mm, "end": v(95.25, -215.9) * mm});
            skLineSegment(sketch, "E125.0", {"start": v(-92.08, -212.72) * mm, "end": v(-95.25, -215.9) * mm});
            skSolve(sketch);
        }
        {
            var Q0;
            Q0=makeQuery(id+"F17.imprint","IMPRINT",FACE,{"disambiguationData":[TD([[makeQuery(id+"F17.imprint","IMPRINT",EDGE,{"derivedFrom":sQuery(id+"F17.wireOp",EDGE,"E94")}),-1.0]])]});
            var Q1;
            Q1=makeQuery(id+"F17.imprint","IMPRINT",FACE,{"disambiguationData":[TD([[makeQuery(id+"F17.imprint","IMPRINT",EDGE,{"derivedFrom":sQuery(id+"F17.wireOp",EDGE,"E109.MirrorCS")}),-1.0]])]});
            extrude(context, id + "F18", {"entities" : qUnion([Q0, Q1]), "operationType" : NewBodyOperationType.ADD, "depth" : 12.7 * mm, "offsetDistance" : 25.4 * mm});
        }
    });
